SOLIDWORKS PART (.sldprt)
format: sldprt  version: not decoded by parser v0  size: 106,496 bytes
history: native  units: mm
features: plane x3, sketch x3, material x1, revolve x1, extrude x1, cut_extrude x1 (+8 scaffold rows collapsed)
feature tree (18):
  scaffold x8  (default folders/planes/origin — collapsed)
  material  "Matériau <non spécifié>"
  plane  "Plan de face"
  plane  "Plan de dessus"
  plane  "Plan de droite"
  sketch  "Esquisse1"  dims[c1.D1=1.5mm c1.D2=4.4mm c1.D3=2.9mm c1.D4=1.0mm c1.D5=1.9mm c2.D2=2.9mm]
  revolve  "Révolution1"  Angle=360deg
  sketch  "Esquisse2"  dims[D1=1.27mm D2=2.54mm]
  extrude  "Extrusion1"  Depth=2mm
  sketch  "Esquisse3"  dims[D1=1.5mm]
  cut_extrude  "Enlèv. mat.-Extru.1"  Depth=4mm
decode coverage: 6 of 6 modeling features carry decoded parameters
note: suppression state not decoded; provenance and decode notes live in map.json
